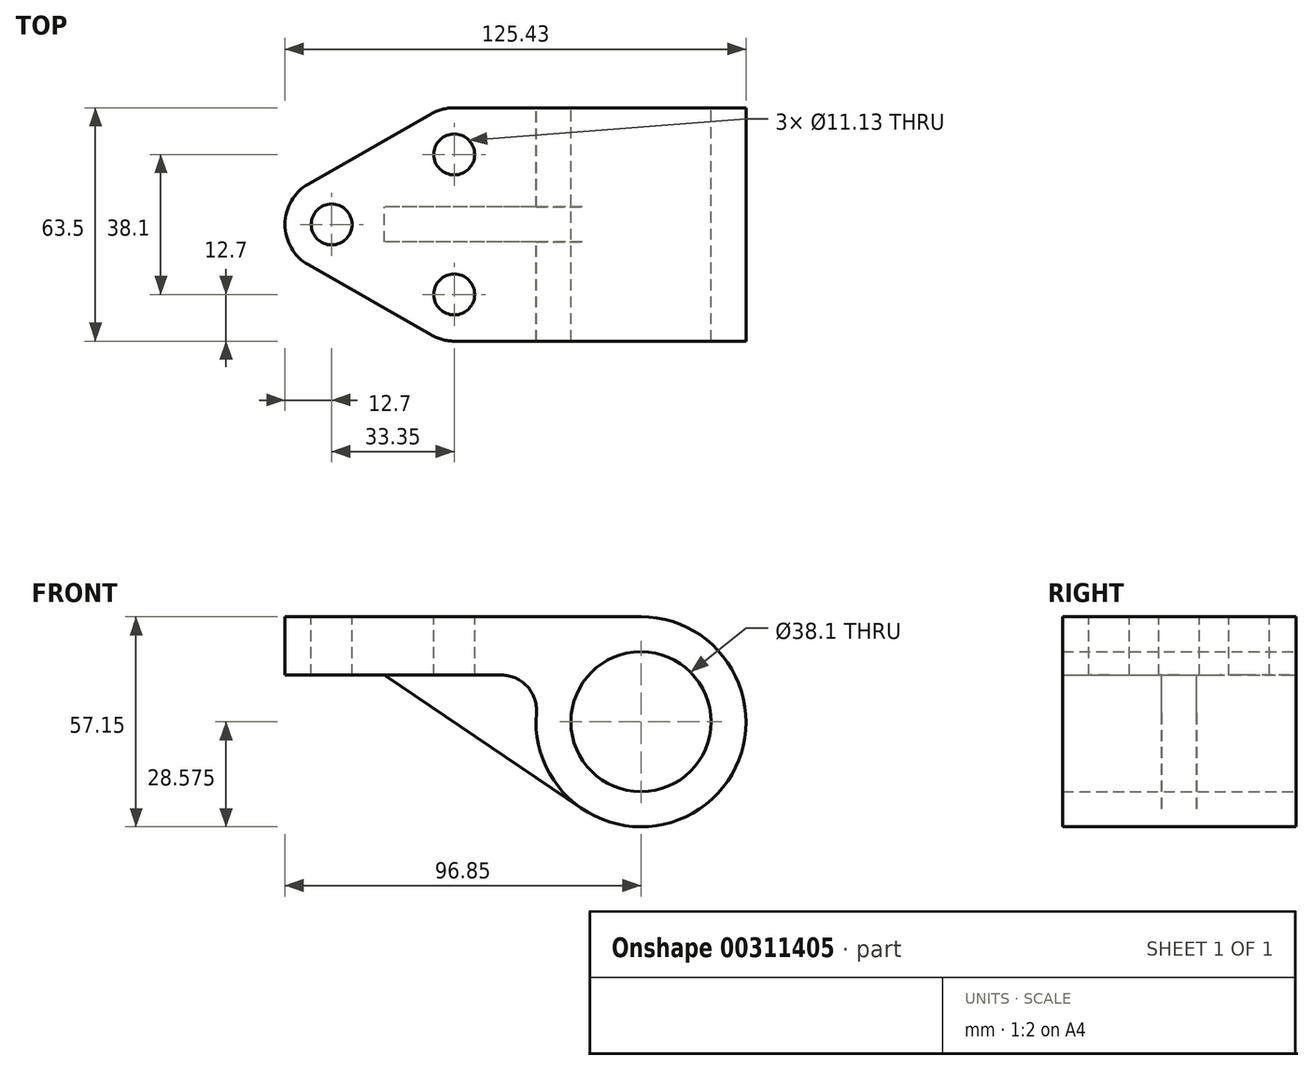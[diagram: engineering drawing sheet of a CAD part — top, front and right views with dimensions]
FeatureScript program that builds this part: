
annotation { "Feature Type Name" : "Feature", "Feature Type Description" : "" }
export const myFeature = defineFeature(function(context is Context, id is Id, definition is map)
    precondition{}
    {
        {
            var Q0;
            Q0=qCreatedBy(makeId("Front.planeOp"),FACE);
            var sketch = newSketch(context, id + "F0", { "sketchPlane" : qUnion([Q0])});
            skLineSegment(sketch, "E0", {"start": v(0, 57.15) * mm, "end": v(96.85, 57.15) * mm});
            skArc(sketch, "E1", {"start": v(96.85, 57.15) * mm, "mid": v(116.2, 7.54) * mm, "end": v(68.37, 30.96) * mm});
            skArc(sketch, "E2", {"start": v(68.37, 30.96) * mm, "mid": v(65.9, 38.2) * mm, "end": v(58.88, 41.28) * mm});
            skLineSegment(sketch, "E3", {"start": v(58.88, 41.28) * mm, "end": v(0, 41.28) * mm});
            skLineSegment(sketch, "E4", {"start": v(0, 41.28) * mm, "end": v(0, 57.15) * mm});
            skCircle(sketch, "E5", {"center": v(96.85, 28.57) * mm, "radius": 19.05 * mm});
            skLineSegment(sketch, "E6", {"start": v(80.86, 4.9) * mm, "end": v(27, 41.28) * mm});
            skSolve(sketch);
        }
        {
            var Q0;
            {var subQ4=sQuery(id+"F0.wireOp",EDGE,"E0");Q0=makeQuery(id+"F0.imprint","IMPRINT",FACE,{"disambiguationData":[TD([[makeQuery(id+"F0.imprint","IMPRINT",EDGE,{"derivedFrom":subQ4}),-1.0]])]});}
            extrude(context, id + "F1", {"entities" : qUnion([Q0]), "endBound" : BoundingType.SYMMETRIC, "depth" : 63.5 * mm, "hasSecondDirection" : true, "secondDirectionOppositeDirection" : true, "secondDirectionDepth" : 25.4 * mm});
        }
        {
            var Q0;
            {var subQ0=sQuery(id+"F0.wireOp",EDGE,"E2");Q0=makeQuery(id+"F0.imprint","IMPRINT",FACE,{"disambiguationData":[TD([[makeQuery(id+"F0.imprint","IMPRINT",EDGE,{"derivedFrom":subQ0}),1.0]])]});}
            extrude(context, id + "F2", {"entities" : qUnion([Q0]), "operationType" : NewBodyOperationType.ADD, "endBound" : BoundingType.SYMMETRIC, "depth" : 9.52 * mm});
        }
        {
            var Q0;
            Q0=makeQuery(id+"F1.opExtrude","SWEPT_FACE",FACE,{"disambiguationData":[OSD([sQuery(id+"F0.wireOp",EDGE,"E0")])]});
            var sketch = newSketch(context, id + "F3", { "sketchPlane" : qUnion([Q0])});
            skCircle(sketch, "E7", {"center": v(46.05, 19.05) * mm, "radius": 5.56 * mm});
            skCircle(sketch, "E8", {"center": v(46.05, -19.05) * mm, "radius": 5.56 * mm});
            skCircle(sketch, "E9", {"center": v(12.7, 0) * mm, "radius": 5.56 * mm});
            skLineSegment(sketch, "E10", {"start": v(6.4, 11.03) * mm, "end": v(39.75, 30.08) * mm});
            skLineSegment(sketch, "E11", {"start": v(6.4, -11.03) * mm, "end": v(39.75, -30.08) * mm});
            skArc(sketch, "E12", {"start": v(6.4, 11.03) * mm, "mid": v(0, 0) * mm, "end": v(6.4, -11.03) * mm});
            skArc(sketch, "E13", {"start": v(58.75, 19.05) * mm, "mid": v(52.43, 30.03) * mm, "end": v(39.75, 30.08) * mm});
            skArc(sketch, "E14", {"start": v(39.75, -30.08) * mm, "mid": v(52.43, -30.03) * mm, "end": v(58.75, -19.05) * mm});
            skLineSegment(sketch, "E15", {"start": v(58.75, 19.05) * mm, "end": v(58.75, -19.05) * mm});
            skSolve(sketch);
        }
        {
            var Q0;
            {var subQ1=sQuery(id+"F3.wireOp",EDGE,"E10");Q0=makeQuery(id+"F3.imprint","IMPRINT",FACE,{"disambiguationData":[TD([[makeQuery(id+"F3.imprint","IMPRINT",EDGE,{"derivedFrom":subQ1}),1.0]])]});}
            var Q1;
            {var subQ1=sQuery(id+"F3.wireOp",EDGE,"E11");Q1=makeQuery(id+"F3.imprint","IMPRINT",FACE,{"disambiguationData":[TD([[makeQuery(id+"F3.imprint","IMPRINT",EDGE,{"derivedFrom":subQ1}),-1.0]])]});}
            extrude(context, id + "F4", {"entities" : qUnion([Q0, Q1]), "operationType" : NewBodyOperationType.REMOVE, "endBound" : BoundingType.THROUGH_ALL, "oppositeDirection" : true, "depth" : 25.4 * mm});
        }
        {
            var Q0;
            Q0=makeQuery(id+"F3.imprint","IMPRINT",FACE,{"disambiguationData":[TD([[makeQuery(id+"F3.imprint","IMPRINT",EDGE,{"derivedFrom":sQuery(id+"F3.wireOp",EDGE,"E9")}),1.0]])]});
            var Q1;
            Q1=makeQuery(id+"F3.imprint","IMPRINT",FACE,{"disambiguationData":[TD([[makeQuery(id+"F3.imprint","IMPRINT",EDGE,{"derivedFrom":sQuery(id+"F3.wireOp",EDGE,"E7")}),1.0]])]});
            var Q2;
            Q2=makeQuery(id+"F3.imprint","IMPRINT",FACE,{"disambiguationData":[TD([[makeQuery(id+"F3.imprint","IMPRINT",EDGE,{"derivedFrom":sQuery(id+"F3.wireOp",EDGE,"E8")}),1.0]])]});
            extrude(context, id + "F5", {"entities" : qUnion([Q0, Q1, Q2]), "operationType" : NewBodyOperationType.REMOVE, "endBound" : BoundingType.THROUGH_ALL, "oppositeDirection" : true, "depth" : 25.4 * mm});
        }
    });
